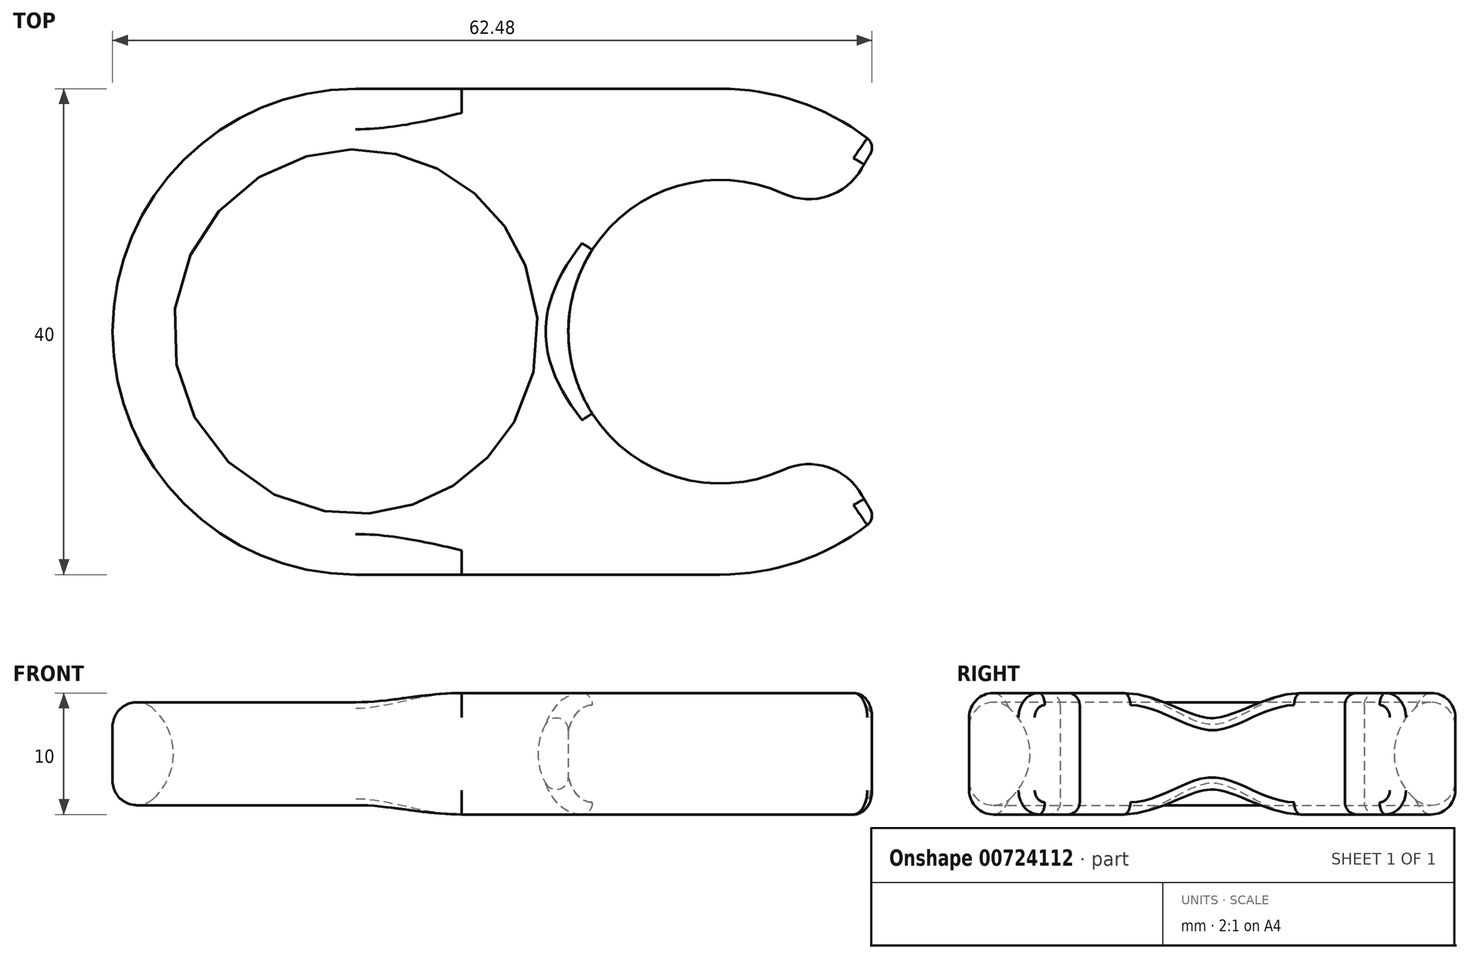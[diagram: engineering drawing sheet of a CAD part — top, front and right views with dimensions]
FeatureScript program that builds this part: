
annotation { "Feature Type Name" : "Feature", "Feature Type Description" : "" }
export const myFeature = defineFeature(function(context is Context, id is Id, definition is map)
    precondition{}
    {
        {
            var Q0;
            Q0=qCreatedBy(makeId("Top.planeOp"),FACE);
            var sketch = newSketch(context, id + "F0", { "sketchPlane" : qUnion([Q0])});
            skLineSegment(sketch, "E0", {"start": v(0, 20) * mm, "end": v(-30, 20) * mm});
            skLineSegment(sketch, "E1", {"start": v(0, -20) * mm, "end": v(-30, -20) * mm});
            skLineSegment(sketch, "E2", {"start": v(-50, 0) * mm, "end": v(-50, 0) * mm});
            skPoint(sketch, "E3.visualSharp", {"position": v(-50, 20) * mm});
            skArc(sketch, "E3.filletArc", {"start": v(-30, 20) * mm, "mid": v(-44.14, 14.14) * mm, "end": v(-50, 0) * mm});
            skPoint(sketch, "E4.visualSharp", {"position": v(-50, -20) * mm});
            skArc(sketch, "E4.filletArc", {"start": v(-50, 0) * mm, "mid": v(-44.14, -14.14) * mm, "end": v(-30, -20) * mm});
            skCircle(sketch, "E5", {"center": v(-30, 0) * mm, "radius": 15 * mm});
            skPoint(sketch, "E6", {"position": v(35.63, 0) * mm});
            skArc(sketch, "E7", {"start": v(12.82, 15.35) * mm, "mid": v(6.82, 18.8) * mm, "end": v(0, 20) * mm});
            skArc(sketch, "E8", {"start": v(5.2, 11.36) * mm, "mid": v(-12.5, 0) * mm, "end": v(5.2, -11.36) * mm});
            skArc(sketch, "E9", {"start": v(11.65, -13.46) * mm, "mid": v(12.22, -14.42) * mm, "end": v(12.82, -15.35) * mm});
            skArc(sketch, "E10.trimOffspring", {"start": v(12.82, 15.35) * mm, "mid": v(12.22, 14.42) * mm, "end": v(11.65, 13.46) * mm});
            skArc(sketch, "E11.trimOffspring", {"start": v(0, -20) * mm, "mid": v(6.82, -18.8) * mm, "end": v(12.82, -15.35) * mm});
            skPoint(sketch, "E12.visualSharp", {"position": v(9.4, -8.24) * mm});
            skArc(sketch, "E12.filletArc", {"start": v(11.65, -13.46) * mm, "mid": v(8.84, -11.15) * mm, "end": v(5.2, -11.36) * mm});
            skPoint(sketch, "E13.visualSharp", {"position": v(9.4, 8.24) * mm});
            skArc(sketch, "E13.filletArc", {"start": v(5.2, 11.36) * mm, "mid": v(8.84, 11.15) * mm, "end": v(11.65, 13.46) * mm});
            skSolve(sketch);
        }
        {
            var Q0;
            Q0=makeQuery(id+"F0.imprint","IMPRINT",FACE,{"disambiguationData":[TD([[makeQuery(id+"F0.imprint","IMPRINT",EDGE,{"derivedFrom":sQuery(id+"F0.wireOp",EDGE,"E0")}),1.0]])]});
            extrude(context, id + "F1", {"entities" : qUnion([Q0]), "depth" : 10 * mm, "offsetDistance" : 25 * mm});
        }
        {
            var Q0;
            Q0=makeQuery(id+"F1.opExtrude","CAP_EDGE",EDGE,{"disambiguationData":[OSD([sQuery(id+"F0.wireOp",EDGE,"E5")])],"isStart":false});
            var Q1;
            Q1=makeQuery(id+"F1.opExtrude","CAP_EDGE",EDGE,{"disambiguationData":[OSD([sQuery(id+"F0.wireOp",EDGE,"E5")])],"isStart":true});
            fillet(context, id + "F2", {"entities" : qUnion([Q0, Q1]), "radius" : 5 * mm, "tangentPropagation" : true, "allowEdgeOverflow" : false});
        }
        {
            var Q0;
            Q0=makeQuery(id+"F2.opFillet","BLEND_EDGE",EDGE,{"blendedFrom":[makeQuery(id+"F1.opExtrude","CAP_EDGE",EDGE,{"disambiguationData":[OSD([sQuery(id+"F0.wireOp",EDGE,"E5")])],"isStart":false}),makeQuery(id+"F1.opExtrude","SWEPT_FACE",FACE,{"disambiguationData":[OSD([sQuery(id+"F0.wireOp",EDGE,"E3.filletArc"),sQuery(id+"F0.wireOp",EDGE,"E4.filletArc")])]})],"blendedInto":[makeQuery(id+"F1.opExtrude","SWEPT_FACE",FACE,{"disambiguationData":[OSD([sQuery(id+"F0.wireOp",EDGE,"E3.filletArc"),sQuery(id+"F0.wireOp",EDGE,"E4.filletArc")])]})]});
            var Q1;
            Q1=makeQuery(id+"F2.opFillet","BLEND_EDGE",EDGE,{"blendedFrom":[makeQuery(id+"F1.opExtrude","CAP_EDGE",EDGE,{"disambiguationData":[OSD([sQuery(id+"F0.wireOp",EDGE,"E5")])],"isStart":true}),makeQuery(id+"F1.opExtrude","SWEPT_FACE",FACE,{"disambiguationData":[OSD([sQuery(id+"F0.wireOp",EDGE,"E3.filletArc"),sQuery(id+"F0.wireOp",EDGE,"E4.filletArc")])]})],"blendedInto":[makeQuery(id+"F1.opExtrude","SWEPT_FACE",FACE,{"disambiguationData":[OSD([sQuery(id+"F0.wireOp",EDGE,"E3.filletArc"),sQuery(id+"F0.wireOp",EDGE,"E4.filletArc")])]})]});
            var Q2;
            Q2=makeQuery(id+"F1.opExtrude","CAP_EDGE",EDGE,{"disambiguationData":[OSD([sQuery(id+"F0.wireOp",EDGE,"E1")])],"isStart":false});
            var Q3;
            Q3=makeQuery(id+"F1.opExtrude","CAP_EDGE",EDGE,{"disambiguationData":[OSD([sQuery(id+"F0.wireOp",EDGE,"E1")])],"isStart":true});
            var Q4;
            Q4=makeQuery(id+"F1.opExtrude","CAP_EDGE",EDGE,{"disambiguationData":[OSD([sQuery(id+"F0.wireOp",EDGE,"E11.trimOffspring")])],"isStart":false});
            var Q5;
            Q5=makeQuery(id+"F1.opExtrude","CAP_EDGE",EDGE,{"disambiguationData":[OSD([sQuery(id+"F0.wireOp",EDGE,"E11.trimOffspring")])],"isStart":true});
            var Q6;
            Q6=makeQuery(id+"F1.opExtrude","CAP_EDGE",EDGE,{"disambiguationData":[OSD([sQuery(id+"F0.wireOp",EDGE,"E7")])],"isStart":false});
            var Q7;
            Q7=makeQuery(id+"F1.opExtrude","CAP_EDGE",EDGE,{"disambiguationData":[OSD([sQuery(id+"F0.wireOp",EDGE,"E0")])],"isStart":false});
            var Q8;
            Q8=makeQuery(id+"F1.opExtrude","CAP_EDGE",EDGE,{"disambiguationData":[OSD([sQuery(id+"F0.wireOp",EDGE,"E0")])],"isStart":true});
            var Q9;
            Q9=makeQuery(id+"F1.opExtrude","CAP_EDGE",EDGE,{"disambiguationData":[OSD([sQuery(id+"F0.wireOp",EDGE,"E7")])],"isStart":true});
            fillet(context, id + "F3", {"entities" : qUnion([Q0, Q1, Q2, Q3, Q4, Q5, Q6, Q7, Q8, Q9]), "radius" : 2 * mm, "tangentPropagation" : true, "allowEdgeOverflow" : false});
        }
        {
            var Q0;
            Q0=makeQuery(id+"F1.opExtrude","SWEPT_EDGE",EDGE,{"disambiguationData":[OSD([sQuery(id+"F0.wireOp",EDGE,"E8"),sQuery(id+"F0.wireOp",EDGE,"E10.trimOffspring")])]});
            var Q1;
            Q1=makeQuery(id+"F1.opExtrude","SWEPT_EDGE",EDGE,{"disambiguationData":[OSD([sQuery(id+"F0.wireOp",EDGE,"E8"),sQuery(id+"F0.wireOp",EDGE,"E9")])]});
            fillet(context, id + "F4", {"entities" : qUnion([Q0, Q1]), "radius" : 1 * mm, "tangentPropagation" : true, "allowEdgeOverflow" : false});
        }
    });
